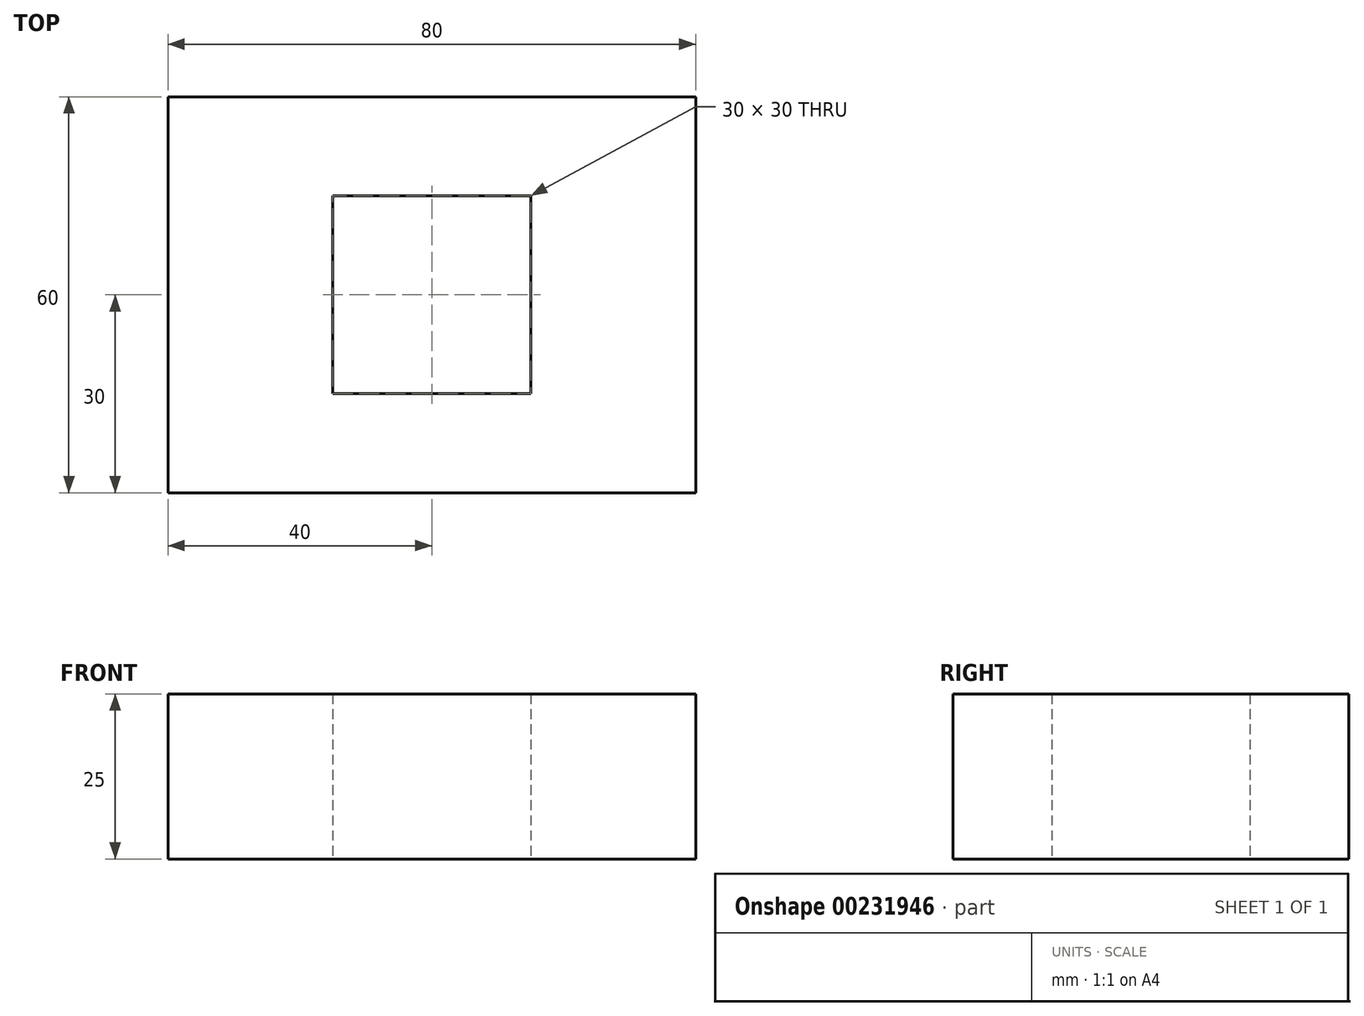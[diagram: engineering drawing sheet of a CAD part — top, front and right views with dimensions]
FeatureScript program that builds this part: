
annotation { "Feature Type Name" : "Feature", "Feature Type Description" : "" }
export const myFeature = defineFeature(function(context is Context, id is Id, definition is map)
    precondition{}
    {
        {
            var Q0;
            Q0=qCreatedBy(makeId("Top.planeOp"),FACE);
            var sketch = newSketch(context, id + "F0", { "sketchPlane" : qUnion([Q0])});
            skLineSegment(sketch, "E0.bottom", {"start": v(0, 0) * mm, "end": v(80, 0) * mm});
            skLineSegment(sketch, "E0.top", {"start": v(0, 60) * mm, "end": v(80, 60) * mm});
            skLineSegment(sketch, "E0.left", {"start": v(0, 0) * mm, "end": v(0, 60) * mm});
            skLineSegment(sketch, "E0.right", {"start": v(80, 0) * mm, "end": v(80, 60) * mm});
            skLineSegment(sketch, "E1.bottom", {"start": v(25, 45) * mm, "end": v(55, 45) * mm});
            skLineSegment(sketch, "E1.top", {"start": v(25, 15) * mm, "end": v(55, 15) * mm});
            skLineSegment(sketch, "E1.left", {"start": v(25, 45) * mm, "end": v(25, 15) * mm});
            skLineSegment(sketch, "E1.right", {"start": v(55, 45) * mm, "end": v(55, 15) * mm});
            skSolve(sketch);
        }
        {
            var Q0;
            Q0=makeQuery(id+"F0.imprint","IMPRINT",FACE,{"disambiguationData":[TD([[makeQuery(id+"F0.imprint","IMPRINT",EDGE,{"derivedFrom":sQuery(id+"F0.wireOp",EDGE,"E0.bottom")}),1.0]])]});
            extrude(context, id + "F1", {"entities" : qUnion([Q0]), "depth" : 25 * mm});
        }
    });
